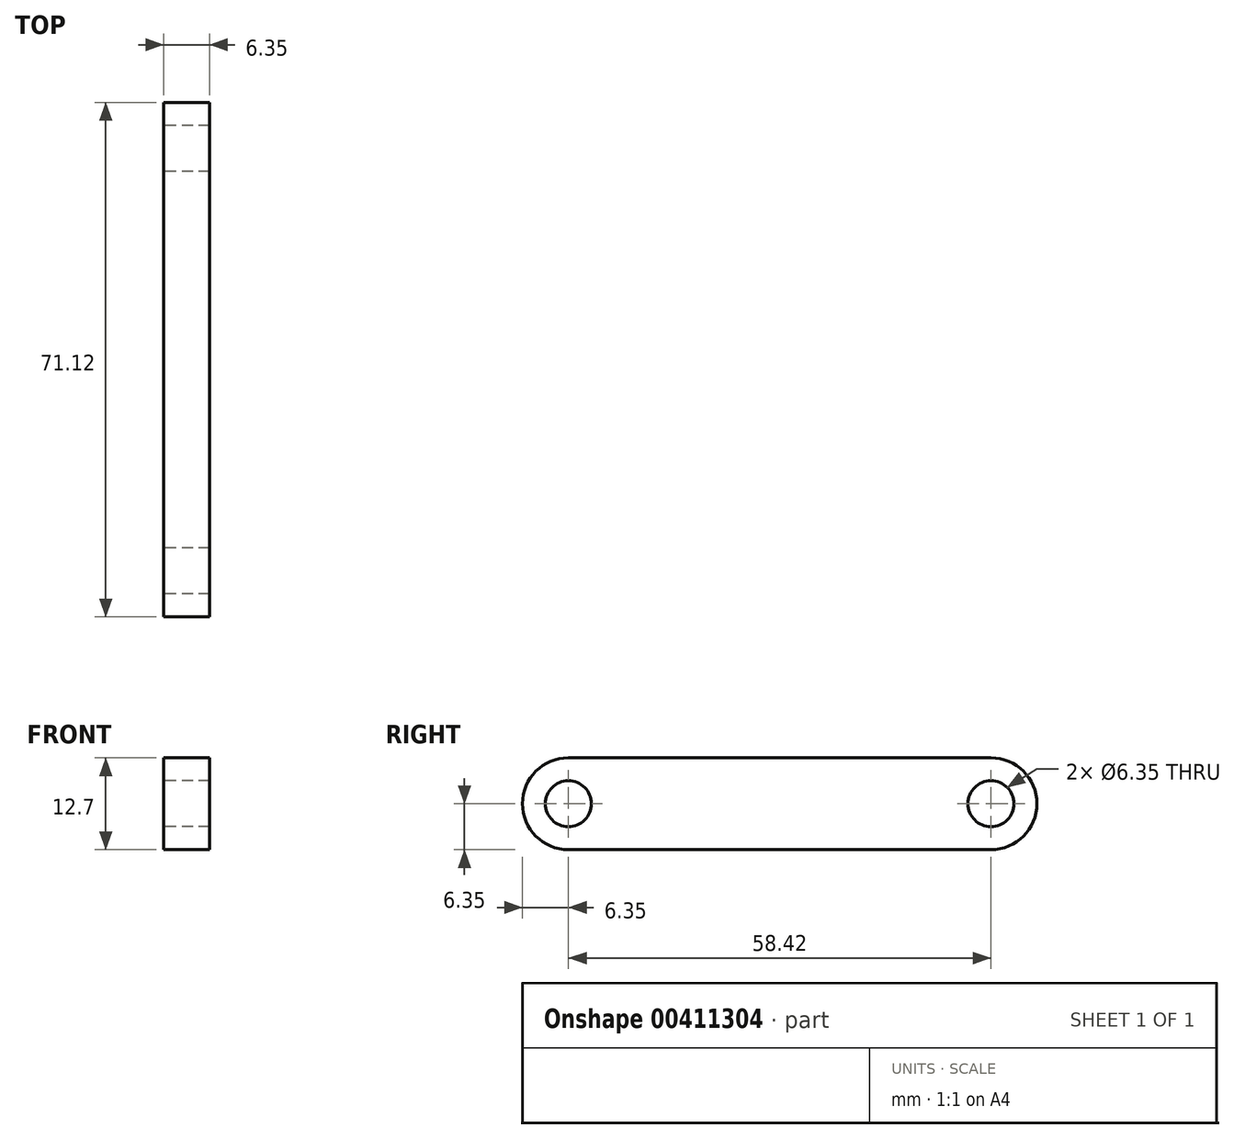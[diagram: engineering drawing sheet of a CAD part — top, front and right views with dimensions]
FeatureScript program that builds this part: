
annotation { "Feature Type Name" : "Feature", "Feature Type Description" : "" }
export const myFeature = defineFeature(function(context is Context, id is Id, definition is map)
    precondition{}
    {
        {
            var Q0;
            Q0=qCreatedBy(makeId("Right.planeOp"),FACE);
            var sketch = newSketch(context, id + "F0", { "sketchPlane" : qUnion([Q0])});
            skLineSegment(sketch, "E0.bottom", {"start": v(0, 6.35) * mm, "end": v(58.42, 6.35) * mm});
            skLineSegment(sketch, "E0.top", {"start": v(0, -6.35) * mm, "end": v(58.42, -6.35) * mm});
            skLineSegment(sketch, "E1", {"start": v(-29.53, 0) * mm, "end": v(77.28, 0) * mm, "construction": true});
            skArc(sketch, "E2", {"start": v(58.42, -6.35) * mm, "mid": v(64.77, 0) * mm, "end": v(58.42, 6.35) * mm});
            skArc(sketch, "E3", {"start": v(0, 6.35) * mm, "mid": v(-6.35, 0) * mm, "end": v(0, -6.35) * mm});
            skCircle(sketch, "E4", {"center": v(0, 0) * mm, "radius": 3.18 * mm});
            skCircle(sketch, "E5", {"center": v(58.42, 0) * mm, "radius": 3.18 * mm});
            skSolve(sketch);
        }
        {
            var Q0;
            Q0 = qSketchRegion(id + "F0", true);
            extrude(context, id + "F1", {"entities" : qUnion([Q0]), "depth" : 6.35 * mm});
        }
    });
